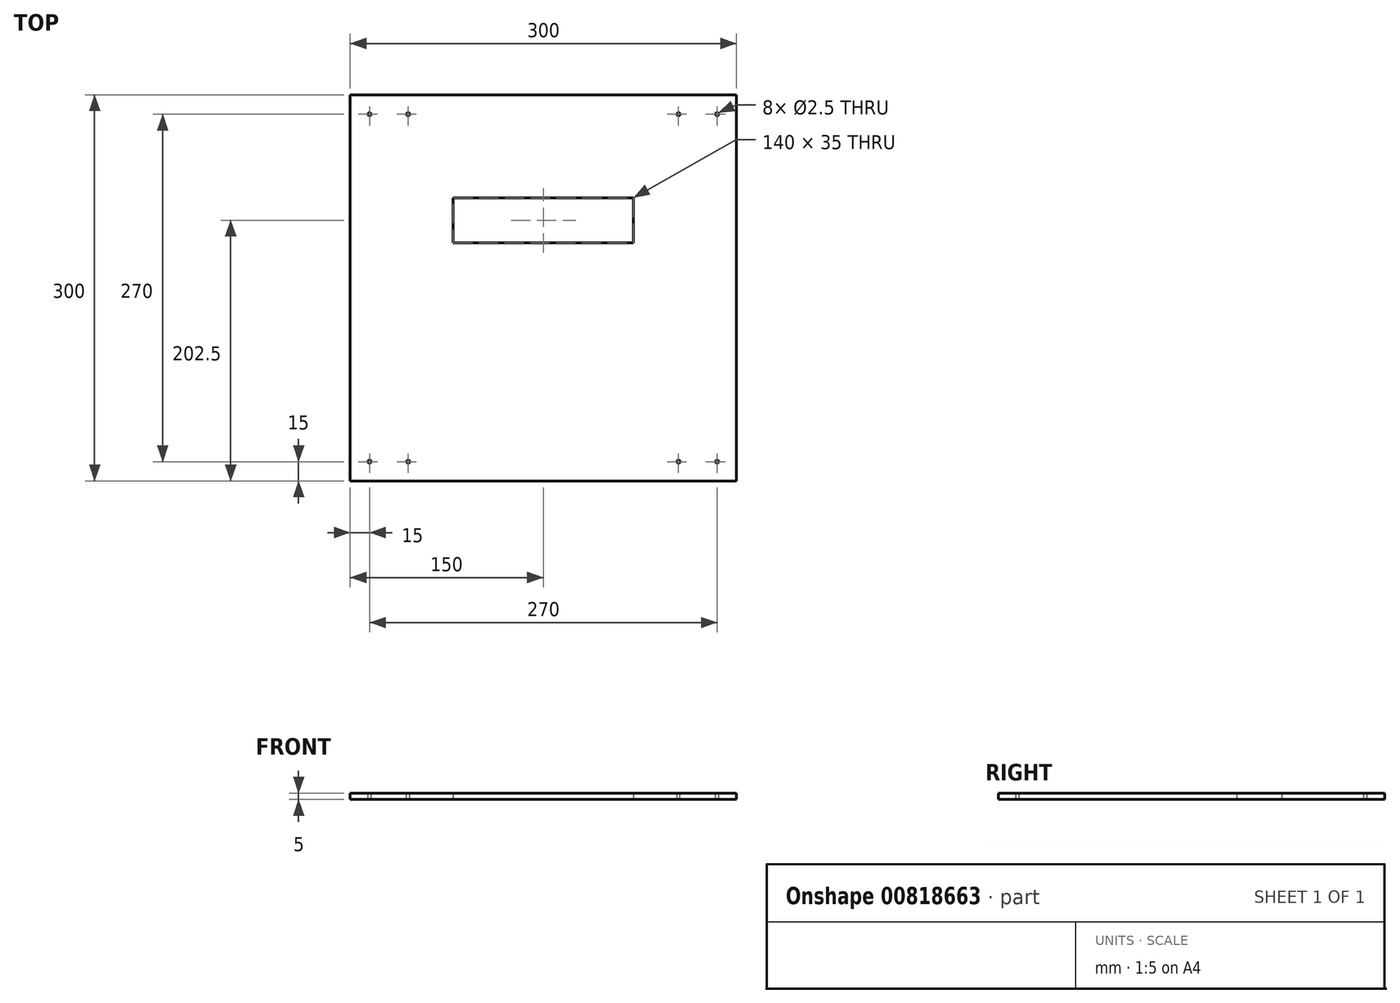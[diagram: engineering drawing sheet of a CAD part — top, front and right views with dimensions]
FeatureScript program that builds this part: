
annotation { "Feature Type Name" : "Feature", "Feature Type Description" : "" }
export const myFeature = defineFeature(function(context is Context, id is Id, definition is map)
    precondition{}
    {
        {
            var Q0;
            Q0=qCreatedBy(makeId("Top.planeOp"),FACE);
            var sketch = newSketch(context, id + "F0", { "sketchPlane" : qUnion([Q0])});
            skLineSegment(sketch, "E0.bottom", {"start": v(-150, 150) * mm, "end": v(150, 150) * mm});
            skLineSegment(sketch, "E0.top", {"start": v(-150, -150) * mm, "end": v(150, -150) * mm});
            skLineSegment(sketch, "E0.left", {"start": v(-150, 150) * mm, "end": v(-150, -150) * mm});
            skLineSegment(sketch, "E0.right", {"start": v(150, 150) * mm, "end": v(150, -150) * mm});
            skPoint(sketch, "E0.middle", {"position": v(0, 0) * mm});
            skLineSegment(sketch, "E1.bottom", {"start": v(-70, 70) * mm, "end": v(70, 70) * mm});
            skLineSegment(sketch, "E1.top", {"start": v(-70, 35) * mm, "end": v(70, 35) * mm});
            skLineSegment(sketch, "E1.left", {"start": v(-70, 70) * mm, "end": v(-70, 35) * mm});
            skLineSegment(sketch, "E1.right", {"start": v(70, 70) * mm, "end": v(70, 35) * mm});
            skSolve(sketch);
        }
        {
            var Q0;
            Q0=makeQuery(id+"F0.imprint","IMPRINT",FACE,{"disambiguationData":[TD([[makeQuery(id+"F0.imprint","IMPRINT",EDGE,{"derivedFrom":sQuery(id+"F0.wireOp",EDGE,"E0.bottom")}),-1.0]])]});
            extrude(context, id + "F1", {"entities" : qUnion([Q0]), "depth" : 5 * mm, "offsetDistance" : 25 * mm});
        }
        {
            var Q0;
            Q0=makeQuery(id+"F1.opExtrude","CAP_FACE",FACE,{"disambiguationData":[OSD([sQuery(id+"F0.wireOp",EDGE,"E0.bottom"),sQuery(id+"F0.wireOp",EDGE,"E0.top"),sQuery(id+"F0.wireOp",EDGE,"E0.left"),sQuery(id+"F0.wireOp",EDGE,"E0.right"),sQuery(id+"F0.wireOp",EDGE,"E1.bottom"),sQuery(id+"F0.wireOp",EDGE,"E1.top"),sQuery(id+"F0.wireOp",EDGE,"E1.left"),sQuery(id+"F0.wireOp",EDGE,"E1.right")])],"isStart":false});
            var sketch = newSketch(context, id + "F2", { "sketchPlane" : qUnion([Q0])});
            skCircle(sketch, "E2", {"center": v(-135, 135) * mm, "radius": 1.25 * mm});
            skCircle(sketch, "E3", {"center": v(135, 135) * mm, "radius": 1.25 * mm});
            skCircle(sketch, "E4", {"center": v(135, -135) * mm, "radius": 1.25 * mm});
            skCircle(sketch, "E5", {"center": v(-135, -135) * mm, "radius": 1.25 * mm});
            skCircle(sketch, "E6", {"center": v(-105, 135) * mm, "radius": 1.25 * mm});
            skCircle(sketch, "E7", {"center": v(105, 135) * mm, "radius": 1.25 * mm});
            skCircle(sketch, "E8", {"center": v(105, -135) * mm, "radius": 1.25 * mm});
            skCircle(sketch, "E9", {"center": v(-105, -135) * mm, "radius": 1.25 * mm});
            skSolve(sketch);
        }
        {
            var Q0;
            Q0=makeQuery(id+"F2.imprint","IMPRINT",FACE,{"disambiguationData":[TD([[makeQuery(id+"F2.imprint","IMPRINT",EDGE,{"derivedFrom":sQuery(id+"F2.wireOp",EDGE,"E2")}),1.0]])]});
            var Q1;
            Q1=makeQuery(id+"F2.imprint","IMPRINT",FACE,{"disambiguationData":[TD([[makeQuery(id+"F2.imprint","IMPRINT",EDGE,{"derivedFrom":sQuery(id+"F2.wireOp",EDGE,"E3")}),1.0]])]});
            var Q2;
            Q2=makeQuery(id+"F2.imprint","IMPRINT",FACE,{"disambiguationData":[TD([[makeQuery(id+"F2.imprint","IMPRINT",EDGE,{"derivedFrom":sQuery(id+"F2.wireOp",EDGE,"E5")}),1.0]])]});
            var Q3;
            Q3=makeQuery(id+"F2.imprint","IMPRINT",FACE,{"disambiguationData":[TD([[makeQuery(id+"F2.imprint","IMPRINT",EDGE,{"derivedFrom":sQuery(id+"F2.wireOp",EDGE,"E4")}),1.0]])]});
            var Q4;
            Q4=makeQuery(id+"F2.imprint","IMPRINT",FACE,{"disambiguationData":[TD([[makeQuery(id+"F2.imprint","IMPRINT",EDGE,{"derivedFrom":sQuery(id+"F2.wireOp",EDGE,"E9")}),1.0]])]});
            var Q5;
            Q5=makeQuery(id+"F2.imprint","IMPRINT",FACE,{"disambiguationData":[TD([[makeQuery(id+"F2.imprint","IMPRINT",EDGE,{"derivedFrom":sQuery(id+"F2.wireOp",EDGE,"E8")}),1.0]])]});
            var Q6;
            Q6=makeQuery(id+"F2.imprint","IMPRINT",FACE,{"disambiguationData":[TD([[makeQuery(id+"F2.imprint","IMPRINT",EDGE,{"derivedFrom":sQuery(id+"F2.wireOp",EDGE,"E7")}),1.0]])]});
            var Q7;
            Q7=makeQuery(id+"F2.imprint","IMPRINT",FACE,{"disambiguationData":[TD([[makeQuery(id+"F2.imprint","IMPRINT",EDGE,{"derivedFrom":sQuery(id+"F2.wireOp",EDGE,"E6")}),1.0]])]});
            extrude(context, id + "F3", {"entities" : qUnion([Q0, Q1, Q2, Q3, Q4, Q5, Q6, Q7]), "operationType" : NewBodyOperationType.REMOVE, "endBound" : BoundingType.THROUGH_ALL, "oppositeDirection" : true, "depth" : 25 * mm, "offsetDistance" : 25 * mm});
        }
    });
